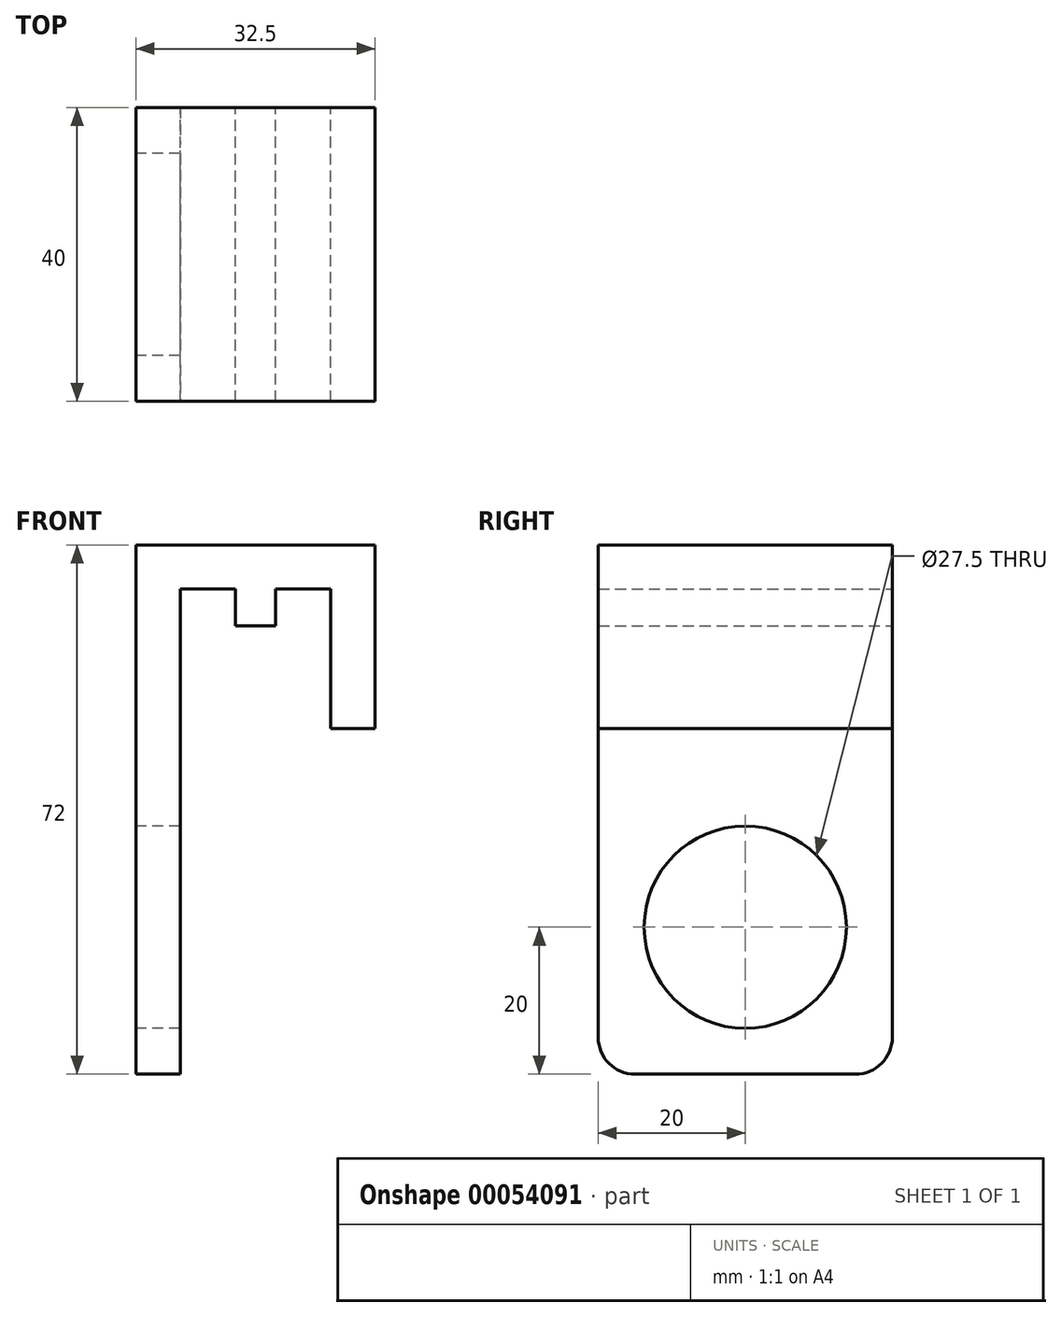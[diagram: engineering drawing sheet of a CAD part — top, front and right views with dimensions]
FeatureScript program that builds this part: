
annotation { "Feature Type Name" : "Feature", "Feature Type Description" : "" }
export const myFeature = defineFeature(function(context is Context, id is Id, definition is map)
    precondition{}
    {
        {
            var Q0;
            Q0=qCreatedBy(makeId("Front.planeOp"),FACE);
            var sketch = newSketch(context, id + "F0", { "sketchPlane" : qUnion([Q0])});
            skLineSegment(sketch, "E0.bottom", {"start": v(0, 0) * mm, "end": v(6, 0) * mm});
            skLineSegment(sketch, "E0.top", {"start": v(0, 72) * mm, "end": v(6, 72) * mm});
            skLineSegment(sketch, "E0.left", {"start": v(0, 0) * mm, "end": v(0, 72) * mm});
            skLineSegment(sketch, "E0.right", {"start": v(6, 0) * mm, "end": v(6, 72) * mm});
            skLineSegment(sketch, "E1.bottom", {"start": v(6, 72) * mm, "end": v(19, 72) * mm});
            skLineSegment(sketch, "E1.top", {"start": v(6, 66) * mm, "end": v(19, 66) * mm});
            skLineSegment(sketch, "E1.left", {"start": v(6, 72) * mm, "end": v(6, 66) * mm});
            skLineSegment(sketch, "E1.right", {"start": v(19, 72) * mm, "end": v(19, 66) * mm});
            skLineSegment(sketch, "E2.bottom", {"start": v(19, 66) * mm, "end": v(13.5, 66) * mm});
            skLineSegment(sketch, "E2.top", {"start": v(19, 61) * mm, "end": v(13.5, 61) * mm});
            skLineSegment(sketch, "E2.left", {"start": v(19, 66) * mm, "end": v(19, 61) * mm});
            skLineSegment(sketch, "E2.right", {"start": v(13.5, 66) * mm, "end": v(13.5, 61) * mm});
            skLineSegment(sketch, "E3.bottom", {"start": v(19, 72) * mm, "end": v(26.5, 72) * mm});
            skLineSegment(sketch, "E3.top", {"start": v(19, 66) * mm, "end": v(26.5, 66) * mm});
            skLineSegment(sketch, "E3.right", {"start": v(26.5, 72) * mm, "end": v(26.5, 66) * mm});
            skLineSegment(sketch, "E4.bottom", {"start": v(26.5, 72) * mm, "end": v(32.5, 72) * mm});
            skLineSegment(sketch, "E4.top", {"start": v(26.5, 47) * mm, "end": v(32.5, 47) * mm});
            skLineSegment(sketch, "E4.left", {"start": v(26.5, 72) * mm, "end": v(26.5, 47) * mm});
            skLineSegment(sketch, "E4.right", {"start": v(32.5, 72) * mm, "end": v(32.5, 47) * mm});
            skSolve(sketch);
        }
        {
            var Q0;
            Q0 = qSketchRegion(id + "F0", true);
            extrude(context, id + "F1", {"entities" : qUnion([Q0]), "depth" : 40 * mm});
        }
        {
            var Q0;
            Q0=makeQuery(id+"F1.opExtrude","CAP_EDGE",EDGE,{"disambiguationData":[OSD([sQuery(id+"F0.wireOp",EDGE,"E0.bottom")])],"isStart":true});
            var Q1;
            Q1=makeQuery(id+"F1.opExtrude","CAP_EDGE",EDGE,{"disambiguationData":[OSD([sQuery(id+"F0.wireOp",EDGE,"E0.bottom")])],"isStart":false});
            fillet(context, id + "F2", {"entities" : qUnion([Q0, Q1]), "radius" : 5 * mm, "tangentPropagation" : true, "allowEdgeOverflow" : false});
        }
        {
            var Q0;
            Q0=makeQuery(id+"F1.opExtrude","SWEPT_FACE",FACE,{"disambiguationData":[OSD([sQuery(id+"F0.wireOp",EDGE,"E0.left")])]});
            var sketch = newSketch(context, id + "F3", { "sketchPlane" : qUnion([Q0])});
            skCircle(sketch, "E5", {"center": v(20, 20) * mm, "radius": 13.75 * mm});
            skSolve(sketch);
        }
        {
            var Q0;
            Q0 = qSketchRegion(id + "F3", true);
            extrude(context, id + "F4", {"entities" : qUnion([Q0]), "operationType" : NewBodyOperationType.REMOVE, "oppositeDirection" : true, "depth" : 25 * mm});
        }
    });
